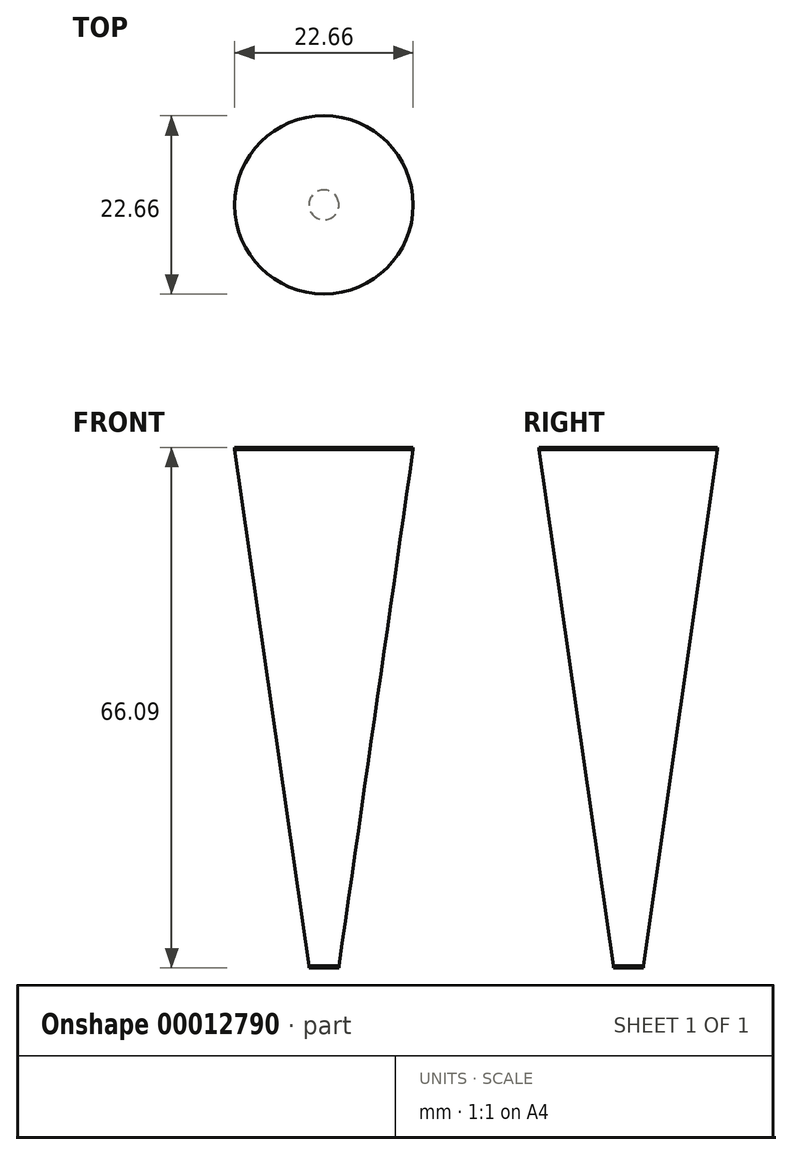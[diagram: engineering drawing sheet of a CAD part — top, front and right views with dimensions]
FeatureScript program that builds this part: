
annotation { "Feature Type Name" : "Feature", "Feature Type Description" : "" }
export const myFeature = defineFeature(function(context is Context, id is Id, definition is map)
    precondition{}
    {
        {
            var Q0;
            Q0=qCreatedBy(makeId("Top.planeOp"),FACE);
            var sketch = newSketch(context, id + "F0", { "sketchPlane" : qUnion([Q0])});
            skCircle(sketch, "E0", {"center": v(0, 0) * mm, "radius": 11.33 * mm});
            skSolve(sketch);
        }
        {
            var Q0;
            Q0=makeQuery(id+"F0.imprint","IMPRINT",FACE,{"disambiguationData":[TD([[makeQuery(id+"F0.imprint","IMPRINT",EDGE,{"derivedFrom":sQuery(id+"F0.wireOp",EDGE,"E0")}),1.0]])]});
            var Q1;
            Q1=sQuery(id+"F0.wireOp",EDGE,"E0");
            extrude(context, id + "F1", {"entities" : qUnion([Q0]), "surfaceEntities" : qUnion([Q1]), "depth" : 0.25 * mm});
        }
        {
            var Q0;
            Q0=qCreatedBy(makeId("Top.planeOp"),FACE);
            var sketch = newSketch(context, id + "F2", { "sketchPlane" : qUnion([Q0])});
            skCircle(sketch, "E1", {"center": v(0, 0) * mm, "radius": 1.9 * mm});
            skSolve(sketch);
        }
        {
            var Q0;
            Q0 = qSketchRegion(id + "F2", true);
            var Q1;
            Q1=sQuery(id+"F2.wireOp",EDGE,"E1");
            extrude(context, id + "F3", {"entities" : qUnion([Q0]), "surfaceEntities" : qUnion([Q1]), "depth" : 0.25 * mm});
        }
        {
            var Q0;
            Q0=makeQuery(id+"F3.opExtrude","SWEPT_BODY",BODY,{"disambiguationData":[OSD([sQuery(id+"F2.wireOp",EDGE,"E1")])]});
            transform(context, id + "F4", {"entities" : qUnion([Q0]), "transformType" : TransformType.TRANSLATION_3D, "dx" : 0 * mm, "dy" : 0 * mm, "dz" : -65.84 * mm, "makeCopy" : false});
        }
        {
            var Q0;
            Q0=makeQuery(id+"F1.opExtrude","CAP_FACE",FACE,{"disambiguationData":[OSD([sQuery(id+"F0.wireOp",EDGE,"E0")])],"isStart":true});
            var Q1;
            Q1=makeQuery(id+"F3.opExtrude","CAP_FACE",FACE,{"disambiguationData":[OSD([sQuery(id+"F2.wireOp",EDGE,"E1")])],"isStart":false});
            loft(context, id + "F5", {"sheetProfilesArray" : [{ "sheetProfileEntities" : qUnion([Q0]) }, { "sheetProfileEntities" : qUnion([Q1]) }]});
        }
    });
